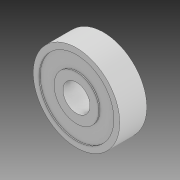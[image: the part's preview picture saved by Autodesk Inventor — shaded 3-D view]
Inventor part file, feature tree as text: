
AUTODESK INVENTOR PART (.ipt)
format: ipt  version: 2020 (Build 240168000, 168)  size: 113,664 bytes
history: native  units: mm
features: extrude x2, sketch x2, mirror x1
ambient origin geometry x8: Origin, YZ Plane, XZ Plane, XY Plane, X Axis, Y Axis, Z Axis, Center Point
bodies: Solid1 (feature_tree)
feature tree (5):
  extrude  "Extrusion1"  Depth=5.0mm
  extrude  "Extrusion2"  Depth=0.2mm TaperAngle=0.0deg
  mirror  "Mirror1"
  sketch  "Sketch1"  dims[d0=16.0mm d1=5.0mm]
  sketch  "Sketch2"  dims[d2=5.0mm d3=0.0mm d4=0.2mm d5=0.0mm]
